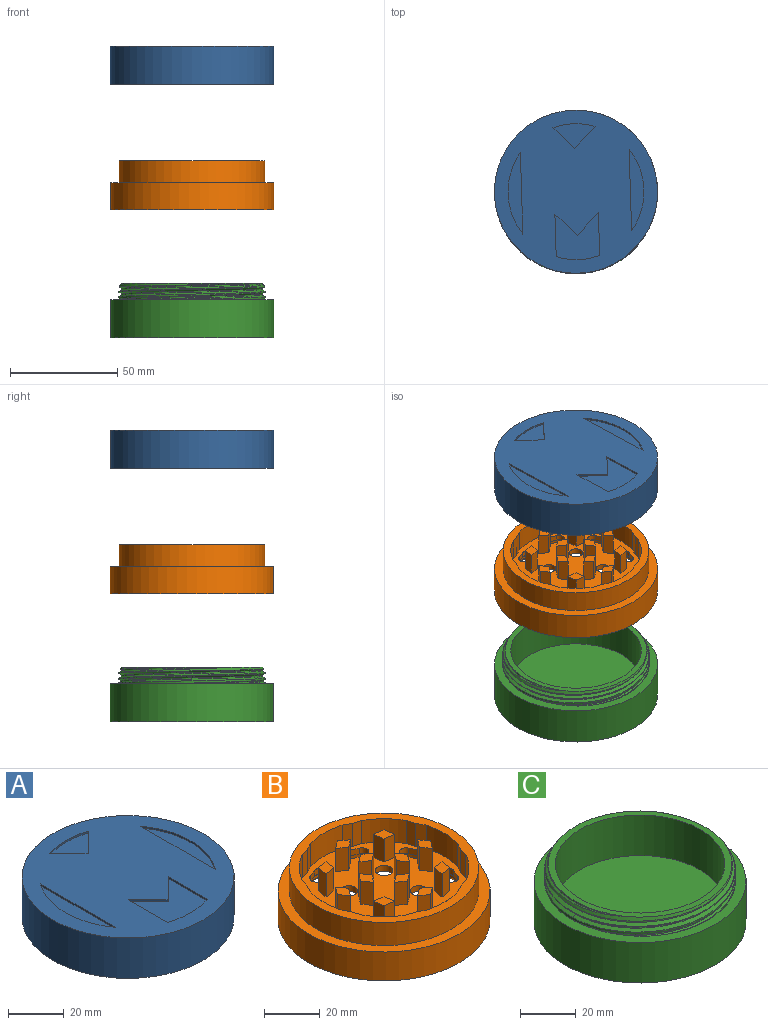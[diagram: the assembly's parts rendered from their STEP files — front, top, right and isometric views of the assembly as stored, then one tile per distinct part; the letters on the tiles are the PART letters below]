
ASSEMBLY  parts=3 mates=2
PART A: 91 faces, bbox 76.2x76.2x17.8 mm
  f0: plane 76.2x76.2mm, normal (0,0,1), area 3788.5mm2, adj f2,f75,f76,f77,f78,f79,f81,f82
  f1: plane 68.58x68.58mm, normal (0,0,-1), area 3405.1mm2, adj f3,f5,f6,f7,f8,f9,f10,f11
  f2: cylinder r=38.1mm len=76.2mm, axis (0,0,1), area 4256.3mm2, adj f0,f4
  f3: cylinder r=34.29mm len=68.58mm, axis (0,0,1), area 2189mm2, adj f1,f4
  f4: plane 76.2x76.2mm, normal (0,0,-1), area 866.5mm2, adj f2,f3
  f5: plane 10.16x3.56mm, normal (-0.92,-0.39,0), area 39.3mm2, adj f1,f6,f13,f14
  f6: cylinder r=2.54mm len=10.16mm, axis (0,0,1), area 20.8mm2, adj f1,f5,f7,f14
  f7: plane 10.16x3.31mm, normal (-0.83,-0.55,0), area 40.3mm2, adj f1,f6,f8,f14
  f8: plane 10.16x3.71mm, normal (0.18,0.98,0), area 38.3mm2, adj f1,f7,f9,f14
  f9: cylinder r=2.54mm len=10.16mm, axis (0,0,1), area 20.8mm2, adj f1,f8,f10,f14
  f10: plane 10.16x3.71mm, normal (-0.18,0.98,0), area 38.3mm2, adj f1,f9,f11,f14
  f11: plane 10.16x3.31mm, normal (0.83,-0.55,0), area 40.3mm2, adj f1,f10,f12,f14
  f12: cylinder r=2.54mm len=10.16mm, axis (0,0,1), area 20.8mm2, adj f1,f11,f13,f14
  f13: plane 10.16x3.56mm, normal (0.92,-0.39,0), area 39.3mm2, adj f1,f5,f12,f14
  f14: plane 9.42x8.6mm, normal (0,0,-1), area 33.3mm2, adj f5,f6,f7,f8,f9,f10,f11,f12
  f15: plane 10.16x3.81mm, normal (0.59,0.81,0), area 48mm2, adj f1,f16,f18,f19
  f16: plane 10.16x3.81mm, normal (0.59,-0.81,0), area 48mm2, adj f1,f15,f17,f19
  f17: plane 10.16x3.81mm, normal (-0.59,-0.81,0), area 48mm2, adj f1,f16,f18,f19
  f18: plane 10.16x3.81mm, normal (-0.59,0.81,0), area 48mm2, adj f1,f15,f17,f19
  f19: plane 7.62x5.59mm, normal (0,0,-1), area 21.3mm2, adj f15,f16,f17,f18
  f20: plane 10.16x3.81mm, normal (0.59,0.81,0), area 48mm2, adj f1,f21,f23,f24
  f21: plane 10.16x3.81mm, normal (0.59,-0.81,0), area 48mm2, adj f1,f20,f22,f24
  f22: plane 10.16x3.81mm, normal (-0.59,-0.81,0), area 48mm2, adj f1,f21,f23,f24
  f23: plane 10.16x3.81mm, normal (-0.59,0.81,0), area 48mm2, adj f1,f20,f22,f24
  f24: plane 7.62x5.59mm, normal (0,0,-1), area 21.3mm2, adj f20,f21,f22,f23
  f25: plane 10.16x4.67mm, normal (-0.15,0.99,0), area 48mm2, adj f1,f26,f28,f29
  f26: plane 10.16x4.67mm, normal (0.99,-0.15,0), area 48mm2, adj f1,f25,f27,f29
  f27: plane 10.16x4.67mm, normal (0.15,-0.99,0), area 48mm2, adj f1,f26,f28,f29
  f28: plane 10.16x4.67mm, normal (-0.99,0.15,0), area 48mm2, adj f1,f25,f27,f29
  f29: plane 5.39x5.39mm, normal (0,0,-1), area 21.3mm2, adj f25,f26,f27,f28
  f30: plane 10.16x3.81mm, normal (-0.81,0.59,0), area 48mm2, adj f1,f31,f33,f34
  f31: plane 10.16x3.81mm, normal (0.81,0.59,0), area 48mm2, adj f1,f30,f32,f34
  f32: plane 10.16x3.81mm, normal (0.81,-0.59,0), area 48mm2, adj f1,f31,f33,f34
  f33: plane 10.16x3.81mm, normal (-0.81,-0.59,0), area 48mm2, adj f1,f30,f32,f34
  f34: plane 7.62x5.59mm, normal (0,0,-1), area 21.3mm2, adj f30,f31,f32,f33
  f35: plane 10.16x4.67mm, normal (-0.99,-0.15,0), area 48mm2, adj f1,f36,f38,f39
  f36: plane 10.16x4.67mm, normal (0.15,0.99,0), area 48mm2, adj f1,f35,f37,f39
  f37: plane 10.16x4.67mm, normal (0.99,0.15,0), area 48mm2, adj f1,f36,f38,f39
  f38: plane 10.16x4.67mm, normal (-0.15,-0.99,0), area 48mm2, adj f1,f35,f37,f39
  f39: plane 5.39x5.39mm, normal (0,0,-1), area 21.3mm2, adj f35,f36,f37,f38
  f40: plane 10.16x3.81mm, normal (-0.59,-0.81,0), area 48mm2, adj f1,f41,f43,f44
  f41: plane 10.16x3.81mm, normal (-0.59,0.81,0), area 48mm2, adj f1,f40,f42,f44
  f42: plane 10.16x3.81mm, normal (0.59,0.81,0), area 48mm2, adj f1,f41,f43,f44
  f43: plane 10.16x3.81mm, normal (0.59,-0.81,0), area 48mm2, adj f1,f40,f42,f44
  f44: plane 7.62x5.59mm, normal (0,0,-1), area 21.3mm2, adj f40,f41,f42,f43
  f45: plane 10.16x4.67mm, normal (0.15,-0.99,0), area 48mm2, adj f1,f46,f48,f49
  f46: plane 10.16x4.67mm, normal (-0.99,0.15,0), area 48mm2, adj f1,f45,f47,f49
  f47: plane 10.16x4.67mm, normal (-0.15,0.99,0), area 48mm2, adj f1,f46,f48,f49
  f48: plane 10.16x4.67mm, normal (0.99,-0.15,0), area 48mm2, adj f1,f45,f47,f49
  f49: plane 5.39x5.39mm, normal (0,0,-1), area 21.3mm2, adj f45,f46,f47,f48
  f50: plane 10.16x3.81mm, normal (0.81,-0.59,0), area 48mm2, adj f1,f51,f53,f54
  f51: plane 10.16x3.81mm, normal (-0.81,-0.59,0), area 48mm2, adj f1,f50,f52,f54
  f52: plane 10.16x3.81mm, normal (-0.81,0.59,0), area 48mm2, adj f1,f51,f53,f54
  f53: plane 10.16x3.81mm, normal (0.81,0.59,0), area 48mm2, adj f1,f50,f52,f54
  f54: plane 7.62x5.59mm, normal (0,0,-1), area 21.3mm2, adj f50,f51,f52,f53
  f55: plane 10.16x4.67mm, normal (0.99,0.15,0), area 48mm2, adj f1,f56,f58,f59
  f56: plane 10.16x4.67mm, normal (-0.15,-0.99,0), area 48mm2, adj f1,f55,f57,f59
  f57: plane 10.16x4.67mm, normal (-0.99,-0.15,0), area 48mm2, adj f1,f56,f58,f59
  f58: plane 10.16x4.67mm, normal (0.15,0.99,0), area 48mm2, adj f1,f55,f57,f59
  f59: plane 5.39x5.39mm, normal (0,0,-1), area 21.3mm2, adj f55,f56,f57,f58
  f60: plane 10.16x3.81mm, normal (-0.81,0.59,0), area 48mm2, adj f1,f61,f63,f64
  f61: plane 10.16x3.81mm, normal (0.81,0.59,0), area 48mm2, adj f1,f60,f62,f64
  f62: plane 10.16x3.81mm, normal (0.81,-0.59,0), area 48mm2, adj f1,f61,f63,f64
  f63: plane 10.16x3.81mm, normal (-0.81,-0.59,0), area 48mm2, adj f1,f60,f62,f64
  f64: plane 7.62x5.59mm, normal (0,0,-1), area 21.3mm2, adj f60,f61,f62,f63
  f65: plane 10.16x3.81mm, normal (-0.59,-0.81,0), area 48mm2, adj f1,f66,f68,f69
  f66: plane 10.16x3.81mm, normal (-0.59,0.81,0), area 48mm2, adj f1,f65,f67,f69
  f67: plane 10.16x3.81mm, normal (0.59,0.81,0), area 48mm2, adj f1,f66,f68,f69
  f68: plane 10.16x3.81mm, normal (0.59,-0.81,0), area 48mm2, adj f1,f65,f67,f69
  f69: plane 7.62x5.59mm, normal (0,0,-1), area 21.3mm2, adj f65,f66,f67,f68
  f70: plane 10.16x3.81mm, normal (0.81,-0.59,0), area 48mm2, adj f1,f71,f73,f74
  f71: plane 10.16x3.81mm, normal (-0.81,-0.59,0), area 48mm2, adj f1,f70,f72,f74
  f72: plane 10.16x3.81mm, normal (-0.81,0.59,0), area 48mm2, adj f1,f71,f73,f74
  f73: plane 10.16x3.81mm, normal (0.81,0.59,0), area 48mm2, adj f1,f70,f72,f74
  f74: plane 7.62x5.59mm, normal (0,0,-1), area 21.3mm2, adj f70,f71,f72,f73
  f75: plane 19.92x0.76mm, normal (-1,0,0), area 15.2mm2, adj f0,f76,f79,f80
  f76: plane 10.16x10.16mm, normal (0.71,-0.71,0), area 10.9mm2, adj f0,f75,f77,f80
  f77: plane 10.16x10.16mm, normal (-0.71,-0.71,0), area 10.9mm2, adj f0,f76,f78,f80
  f78: plane 19.92x0.76mm, normal (1,0,0), area 15.2mm2, adj f0,f77,f79,f80
  f79: cylinder r=31.75mm len=20.32mm, axis (0,0,1), area 15.8mm2, adj f0,f75,f78,f80
  f80: plane 21.59x20.32mm, normal (0,0,1), area 324.3mm2, adj f75,f76,f77,f78,f79
  f81: plane 38.1x0.76mm, normal (-1,0,0), area 29mm2, adj f0,f82,f83
  f82: cylinder r=31.75mm len=38.1mm, axis (0,0,1), area 31.1mm2, adj f0,f81,f83
  f83: plane 38.1x6.35mm, normal (0,0,1), area 164.8mm2, adj f81,f82
  f84: plane 38.1x0.76mm, normal (1,0,0), area 29mm2, adj f0,f85,f86
  f85: cylinder r=31.75mm len=38.1mm, axis (0,0,1), area 31.1mm2, adj f0,f84,f86
  f86: plane 38.1x6.35mm, normal (0,0,1), area 164.8mm2, adj f84,f85
  f87: plane 9.86x9.86mm, normal (-0.71,0.71,0), area 10.6mm2, adj f0,f88,f89,f90
  f88: cylinder r=31.75mm len=19.72mm, axis (0,0,1), area 15.3mm2, adj f0,f87,f89,f90
  f89: plane 9.86x9.86mm, normal (0.71,0.71,0), area 10.6mm2, adj f0,f87,f88,f90
  f90: plane 19.72x11.43mm, normal (0,0,1), area 118mm2, adj f87,f88,f89
PART B: 129 faces, bbox 76.2x76.2x22.9 mm
  f0: cylinder r=30.48mm len=11.39mm, axis (0,0,-1), area 165.6mm2, adj f7,f15,f26,f91
  f1: cylinder r=30.48mm len=16.11mm, axis (0,0,-1), area 165.6mm2, adj f7,f15,f89,f90
  f2: cylinder r=30.48mm len=11.39mm, axis (0,0,-1), area 165.6mm2, adj f7,f15,f87,f88
  f3: cylinder r=30.48mm len=16.11mm, axis (0,0,-1), area 165.6mm2, adj f7,f15,f85,f86
  f4: cylinder r=30.48mm len=11.39mm, axis (0,0,-1), area 165.6mm2, adj f7,f15,f83,f84
  f5: cylinder r=30.48mm len=16.11mm, axis (0,0,-1), area 165.6mm2, adj f7,f15,f81,f82
  f6: cylinder r=30.48mm len=11.39mm, axis (0,0,-1), area 165.6mm2, adj f7,f15,f79,f80
  f7: plane 60.96x60.96mm, normal (0,0,1), area 2197.7mm2, adj f0,f1,f2,f3,f4,f5,f6,f13
  f8: cylinder r=38.1mm len=76.2mm, axis (0,0,-1), area 3040.2mm2, adj f9,f11
  f9: plane 76.2x76.2mm, normal (0,0,1), area 921mm2, adj f8,f14
  f10: cylinder r=34.54mm len=69.09mm, axis (0,0,1), area 1968.1mm2, adj f12,f92
  f11: plane 76.2x76.2mm, normal (0,0,-1), area 672.5mm2, adj f8,f92
  f12: plane 69.09x69.09mm, normal (0,0,-1), area 3305.2mm2, adj f10,f93,f94,f95,f96,f97,f98,f99
  f13: cylinder r=30.48mm len=16.11mm, axis (0,0,-1), area 165.6mm2, adj f7,f15,f27,f78
  f14: cylinder r=34.04mm len=68.07mm, axis (0,0,-1), area 2172.8mm2, adj f9,f15
  f15: plane 68.07x68.07mm, normal (0,0,1), area 742.5mm2, adj f0,f1,f2,f3,f4,f5,f6,f13
  f16: plane 10.16x3.81mm, normal (0.59,-0.81,0), area 48mm2, adj f7,f17,f19,f20
  f17: plane 10.16x3.81mm, normal (0.59,0.81,0), area 48mm2, adj f7,f16,f18,f20
  f18: plane 10.16x3.81mm, normal (-0.59,0.81,0), area 48mm2, adj f7,f17,f19,f20
  f19: plane 10.16x3.81mm, normal (-0.59,-0.81,0), area 48mm2, adj f7,f16,f18,f20
  f20: plane 7.62x5.59mm, normal (0,0,1), area 21.3mm2, adj f16,f17,f18,f19
  f21: plane 10.16x3.81mm, normal (0.59,-0.81,0), area 48mm2, adj f7,f22,f24,f25
  f22: plane 10.16x3.81mm, normal (0.59,0.81,0), area 48mm2, adj f7,f21,f23,f25
  f23: plane 10.16x3.81mm, normal (-0.59,0.81,0), area 48mm2, adj f7,f22,f24,f25
  f24: plane 10.16x3.81mm, normal (-0.59,-0.81,0), area 48mm2, adj f7,f21,f23,f25
  f25: plane 7.62x5.59mm, normal (0,0,1), area 21.3mm2, adj f21,f22,f23,f24
  f26: plane 10.16x3.67mm, normal (0.29,-0.96,0), area 38.9mm2, adj f0,f7,f15,f27
  f27: plane 10.16x3.37mm, normal (0.48,-0.88,0), area 38.9mm2, adj f7,f13,f15,f26
  f28: plane 10.16x4.67mm, normal (0.99,-0.15,0), area 48mm2, adj f7,f29,f31,f32
  f29: plane 10.16x4.67mm, normal (-0.15,0.99,0), area 48mm2, adj f7,f28,f30,f32
  f30: plane 10.16x4.67mm, normal (-0.99,0.15,0), area 48mm2, adj f7,f29,f31,f32
  f31: plane 10.16x4.67mm, normal (0.15,-0.99,0), area 48mm2, adj f7,f28,f30,f32
  f32: plane 5.39x5.39mm, normal (0,0,1), area 21.3mm2, adj f28,f29,f30,f31
  f33: plane 10.16x3.81mm, normal (0.81,0.59,0), area 48mm2, adj f7,f34,f36,f37
  f34: plane 10.16x3.81mm, normal (-0.81,0.59,0), area 48mm2, adj f7,f33,f35,f37
  f35: plane 10.16x3.81mm, normal (-0.81,-0.59,0), area 48mm2, adj f7,f34,f36,f37
  f36: plane 10.16x3.81mm, normal (0.81,-0.59,0), area 48mm2, adj f7,f33,f35,f37
  f37: plane 7.62x5.59mm, normal (0,0,1), area 21.3mm2, adj f33,f34,f35,f36
  f38: plane 10.16x4.67mm, normal (0.15,0.99,0), area 48mm2, adj f7,f39,f41,f42
  f39: plane 10.16x4.67mm, normal (-0.99,-0.15,0), area 48mm2, adj f7,f38,f40,f42
  f40: plane 10.16x4.67mm, normal (-0.15,-0.99,0), area 48mm2, adj f7,f39,f41,f42
  f41: plane 10.16x4.67mm, normal (0.99,0.15,0), area 48mm2, adj f7,f38,f40,f42
  f42: plane 5.39x5.39mm, normal (0,0,1), area 21.3mm2, adj f38,f39,f40,f41
  f43: plane 10.16x3.81mm, normal (-0.59,0.81,0), area 48mm2, adj f7,f44,f46,f47
  f44: plane 10.16x3.81mm, normal (-0.59,-0.81,0), area 48mm2, adj f7,f43,f45,f47
  f45: plane 10.16x3.81mm, normal (0.59,-0.81,0), area 48mm2, adj f7,f44,f46,f47
  f46: plane 10.16x3.81mm, normal (0.59,0.81,0), area 48mm2, adj f7,f43,f45,f47
  f47: plane 7.62x5.59mm, normal (0,0,1), area 21.3mm2, adj f43,f44,f45,f46
  f48: plane 10.16x4.67mm, normal (-0.99,0.15,0), area 48mm2, adj f7,f49,f51,f52
  f49: plane 10.16x4.67mm, normal (0.15,-0.99,0), area 48mm2, adj f7,f48,f50,f52
  f50: plane 10.16x4.67mm, normal (0.99,-0.15,0), area 48mm2, adj f7,f49,f51,f52
  f51: plane 10.16x4.67mm, normal (-0.15,0.99,0), area 48mm2, adj f7,f48,f50,f52
  f52: plane 5.39x5.39mm, normal (0,0,1), area 21.3mm2, adj f48,f49,f50,f51
  f53: plane 10.16x3.81mm, normal (-0.81,-0.59,0), area 48mm2, adj f7,f54,f56,f57
  f54: plane 10.16x3.81mm, normal (0.81,-0.59,0), area 48mm2, adj f7,f53,f55,f57
  f55: plane 10.16x3.81mm, normal (0.81,0.59,0), area 48mm2, adj f7,f54,f56,f57
  f56: plane 10.16x3.81mm, normal (-0.81,0.59,0), area 48mm2, adj f7,f53,f55,f57
  f57: plane 7.62x5.59mm, normal (0,0,1), area 21.3mm2, adj f53,f54,f55,f56
  f58: plane 10.16x4.67mm, normal (-0.15,-0.99,0), area 48mm2, adj f7,f59,f61,f62
  f59: plane 10.16x4.67mm, normal (0.99,0.15,0), area 48mm2, adj f7,f58,f60,f62
  f60: plane 10.16x4.67mm, normal (0.15,0.99,0), area 48mm2, adj f7,f59,f61,f62
  f61: plane 10.16x4.67mm, normal (-0.99,-0.15,0), area 48mm2, adj f7,f58,f60,f62
  f62: plane 5.39x5.39mm, normal (0,0,1), area 21.3mm2, adj f58,f59,f60,f61
  f63: plane 10.16x3.81mm, normal (0.81,0.59,0), area 48mm2, adj f7,f64,f66,f67
  f64: plane 10.16x3.81mm, normal (-0.81,0.59,0), area 48mm2, adj f7,f63,f65,f67
  f65: plane 10.16x3.81mm, normal (-0.81,-0.59,0), area 48mm2, adj f7,f64,f66,f67
  f66: plane 10.16x3.81mm, normal (0.81,-0.59,0), area 48mm2, adj f7,f63,f65,f67
  f67: plane 7.62x5.59mm, normal (0,0,1), area 21.3mm2, adj f63,f64,f65,f66
  f68: plane 10.16x3.81mm, normal (-0.59,0.81,0), area 48mm2, adj f7,f69,f71,f72
  f69: plane 10.16x3.81mm, normal (-0.59,-0.81,0), area 48mm2, adj f7,f68,f70,f72
  f70: plane 10.16x3.81mm, normal (0.59,-0.81,0), area 48mm2, adj f7,f69,f71,f72
  f71: plane 10.16x3.81mm, normal (0.59,0.81,0), area 48mm2, adj f7,f68,f70,f72
  f72: plane 7.62x5.59mm, normal (0,0,1), area 21.3mm2, adj f68,f69,f70,f71
  f73: plane 10.16x3.81mm, normal (-0.81,-0.59,0), area 48mm2, adj f7,f74,f76,f77
  f74: plane 10.16x3.81mm, normal (0.81,-0.59,0), area 48mm2, adj f7,f73,f75,f77
  f75: plane 10.16x3.81mm, normal (0.81,0.59,0), area 48mm2, adj f7,f74,f76,f77
  f76: plane 10.16x3.81mm, normal (-0.81,0.59,0), area 48mm2, adj f7,f73,f75,f77
  f77: plane 7.62x5.59mm, normal (0,0,1), area 21.3mm2, adj f73,f74,f75,f76
  f78: plane 10.16x3.37mm, normal (-0.48,-0.88,0), area 38.9mm2, adj f7,f13,f15,f79
  f79: plane 10.16x3.67mm, normal (-0.29,-0.96,0), area 38.9mm2, adj f6,f7,f15,f78
  f80: plane 10.16x3.67mm, normal (-0.96,-0.29,0), area 38.9mm2, adj f6,f7,f15,f81
  f81: plane 10.16x3.37mm, normal (-0.88,-0.48,0), area 38.9mm2, adj f5,f7,f15,f80
  f82: plane 10.16x3.37mm, normal (-0.88,0.48,0), area 38.9mm2, adj f5,f7,f15,f83
  f83: plane 10.16x3.67mm, normal (-0.96,0.29,0), area 38.9mm2, adj f4,f7,f15,f82
  f84: plane 10.16x3.67mm, normal (-0.29,0.96,0), area 38.9mm2, adj f4,f7,f15,f85
  f85: plane 10.16x3.37mm, normal (-0.48,0.88,0), area 38.9mm2, adj f3,f7,f15,f84
  f86: plane 10.16x3.37mm, normal (0.48,0.88,0), area 38.9mm2, adj f3,f7,f15,f87
  f87: plane 10.16x3.67mm, normal (0.29,0.96,0), area 38.9mm2, adj f2,f7,f15,f86
  f88: plane 10.16x3.67mm, normal (0.96,0.29,0), area 38.9mm2, adj f2,f7,f15,f89
  f89: plane 10.16x3.37mm, normal (0.88,0.48,0), area 38.9mm2, adj f1,f7,f15,f88
  f90: plane 10.16x3.37mm, normal (0.88,-0.48,0), area 38.9mm2, adj f1,f7,f15,f91
  f91: plane 10.16x3.67mm, normal (0.96,-0.29,0), area 38.9mm2, adj f0,f7,f15,f90
  f92: cone r=35.18mm half-angle=30.2deg, axis (0,0,-1), area 276.7mm2, adj f10,f11
  f93: cylinder r=3.17mm len=6.35mm, axis (0,0,1), area 50.7mm2, adj f7,f12
  f94: cylinder r=2.54mm len=4.89mm, axis (0,0,1), area 20.3mm2, adj f7,f12,f95,f97
  f95: plane 3.52x2.54mm, normal (-0.38,0.92,0), area 9.7mm2, adj f7,f12,f94,f96
  f96: cylinder r=2.54mm len=4.89mm, axis (0,0,1), area 20.3mm2, adj f7,f12,f95,f97
  f97: plane 3.52x2.54mm, normal (0.38,-0.92,0), area 9.7mm2, adj f7,f12,f94,f96
  f98: cylinder r=3.17mm len=6.35mm, axis (0,0,1), area 50.7mm2, adj f7,f12
  f99: cylinder r=3.17mm len=6.35mm, axis (0,0,1), area 50.7mm2, adj f7,f12
  f100: cylinder r=3.17mm len=6.35mm, axis (0,0,1), area 50.7mm2, adj f7,f12
  f101: cylinder r=2.54mm len=4.89mm, axis (0,0,1), area 20.3mm2, adj f7,f12,f102,f104
  f102: plane 3.52x2.54mm, normal (0.38,0.92,0), area 9.7mm2, adj f7,f12,f101,f103
  f103: cylinder r=2.54mm len=4.89mm, axis (0,0,1), area 20.3mm2, adj f7,f12,f102,f104
  f104: plane 3.52x2.54mm, normal (-0.38,-0.92,0), area 9.7mm2, adj f7,f12,f101,f103
  f105: cylinder r=2.54mm len=4.89mm, axis (0,0,1), area 20.3mm2, adj f7,f12,f106,f108
  f106: plane 3.52x2.54mm, normal (0.92,0.38,0), area 9.7mm2, adj f7,f12,f105,f107
  f107: cylinder r=2.54mm len=4.89mm, axis (0,0,1), area 20.3mm2, adj f7,f12,f106,f108
  f108: plane 3.52x2.54mm, normal (-0.92,-0.38,0), area 9.7mm2, adj f7,f12,f105,f107
  f109: cylinder r=2.54mm len=4.89mm, axis (0,0,1), area 20.3mm2, adj f7,f12,f110,f112
  f110: plane 3.52x2.54mm, normal (0.92,-0.38,0), area 9.7mm2, adj f7,f12,f109,f111
  f111: cylinder r=2.54mm len=4.89mm, axis (0,0,1), area 20.3mm2, adj f7,f12,f110,f112
  f112: plane 3.52x2.54mm, normal (-0.92,0.38,0), area 9.7mm2, adj f7,f12,f109,f111
  f113: cylinder r=2.54mm len=4.89mm, axis (0,0,1), area 20.3mm2, adj f7,f12,f114,f116
  f114: plane 3.52x2.54mm, normal (0.38,-0.92,0), area 9.7mm2, adj f7,f12,f113,f115
  f115: cylinder r=2.54mm len=4.89mm, axis (0,0,1), area 20.3mm2, adj f7,f12,f114,f116
  f116: plane 3.52x2.54mm, normal (-0.38,0.92,0), area 9.7mm2, adj f7,f12,f113,f115
  f117: cylinder r=2.54mm len=4.89mm, axis (0,0,1), area 20.3mm2, adj f7,f12,f118,f120
  f118: plane 3.52x2.54mm, normal (-0.38,-0.92,0), area 9.7mm2, adj f7,f12,f117,f119
  f119: cylinder r=2.54mm len=4.89mm, axis (0,0,1), area 20.3mm2, adj f7,f12,f118,f120
  f120: plane 3.52x2.54mm, normal (0.38,0.92,0), area 9.7mm2, adj f7,f12,f117,f119
  f121: cylinder r=2.54mm len=4.89mm, axis (0,0,1), area 20.3mm2, adj f7,f12,f122,f124
  f122: plane 3.52x2.54mm, normal (-0.92,-0.38,0), area 9.7mm2, adj f7,f12,f121,f123
  f123: cylinder r=2.54mm len=4.89mm, axis (0,0,1), area 20.3mm2, adj f7,f12,f122,f124
  f124: plane 3.52x2.54mm, normal (0.92,0.38,0), area 9.7mm2, adj f7,f12,f121,f123
  f125: cylinder r=2.54mm len=4.89mm, axis (0,0,1), area 20.3mm2, adj f7,f12,f126,f128
  f126: plane 3.52x2.54mm, normal (-0.92,0.38,0), area 9.7mm2, adj f7,f12,f125,f127
  f127: cylinder r=2.54mm len=4.89mm, axis (0,0,1), area 20.3mm2, adj f7,f12,f126,f128
  f128: plane 3.52x2.54mm, normal (0.92,-0.38,0), area 9.7mm2, adj f7,f12,f125,f127
PART C: 22 faces, bbox 76.7x79.7x26.9 mm
  f0: cylinder r=34.29mm len=68.58mm, axis (0,0,-1), area 145.4mm2, adj f4,f9,f10,f14,f17,f21
  f1: cone r=33.02mm half-angle=29.9deg, axis (0,0,-1), area 111.6mm2, adj f5,f7,f15,f20
  f2: cylinder r=38.1mm len=76.2mm, axis (0,0,-1), area 4256.3mm2, adj f3,f4
  f3: plane 76.2x76.2mm, normal (0,0,-1), area 4560.4mm2, adj f2
  f4: plane 76.28x76.28mm, normal (0,0,1), area 885.6mm2, adj f0,f2,f5,f10,f11,f12,f16,f17
  f5: cylinder r=34.29mm len=68.58mm, axis (0,0,-1), area 145.4mm2, adj f1,f4,f11,f15,f16,f20
  f6: cylinder r=30.48mm len=60.96mm, axis (0,0,-1), area 3405.1mm2, adj f7,f8
  f7: plane 66.54x66.12mm, normal (0,0,1), area 495.8mm2, adj f1,f6,f9,f13,f14,f15,f19,f20
  f8: plane 60.96x60.96mm, normal (0,0,1), area 2918.6mm2, adj f6
  f9: cone r=33.02mm half-angle=29.9deg, axis (0,0,-1), area 111.6mm2, adj f0,f7,f14,f21
  f10: bspline ~70.14x56.2mm, area 91.4mm2, adj f0,f4,f12,f14
  f11: bspline ~69.62x35.19mm, area 83.3mm2, adj f4,f5,f12,f15
  f12: bspline ~67.38x54.01mm, area 70.1mm2, adj f4,f10,f11,f13
  f13: bspline ~76.01x65.83mm, area 151.1mm2, adj f7,f12,f14,f15
  f14: bspline ~79.19x68.58mm, area 230.5mm2, adj f0,f7,f9,f10,f13
  f15: bspline ~79.19x68.58mm, area 324.6mm2, adj f1,f5,f7,f11,f13
  f16: bspline ~70.14x56.2mm, area 91.4mm2, adj f4,f5,f18,f20
  f17: bspline ~69.62x35.19mm, area 83.3mm2, adj f0,f4,f18,f21
  f18: bspline ~67.38x54.01mm, area 70.1mm2, adj f4,f16,f17,f19
  f19: bspline ~76.01x65.83mm, area 151.1mm2, adj f7,f18,f20,f21
  f20: bspline ~79.19x68.58mm, area 230.5mm2, adj f1,f5,f7,f16,f19
  f21: bspline ~79.19x68.58mm, area 324.6mm2, adj f0,f7,f9,f17,f19
PLACE A rot(axis=(0,0,1),1.8deg) t=(0,0,135.99)mm
PLACE B rot(axis=(0,-0.03,1),0deg) t=(0,0,69.78)mm
PLACE C at identity fixed
MATE cylindrical B.f14 <-> A.f2  axis (0,0,-1) through (0,0,77.4)mm
MATE slider B.f8 <-> C.f2  axis (0,0,-1) through (0,0,65.97)mm
